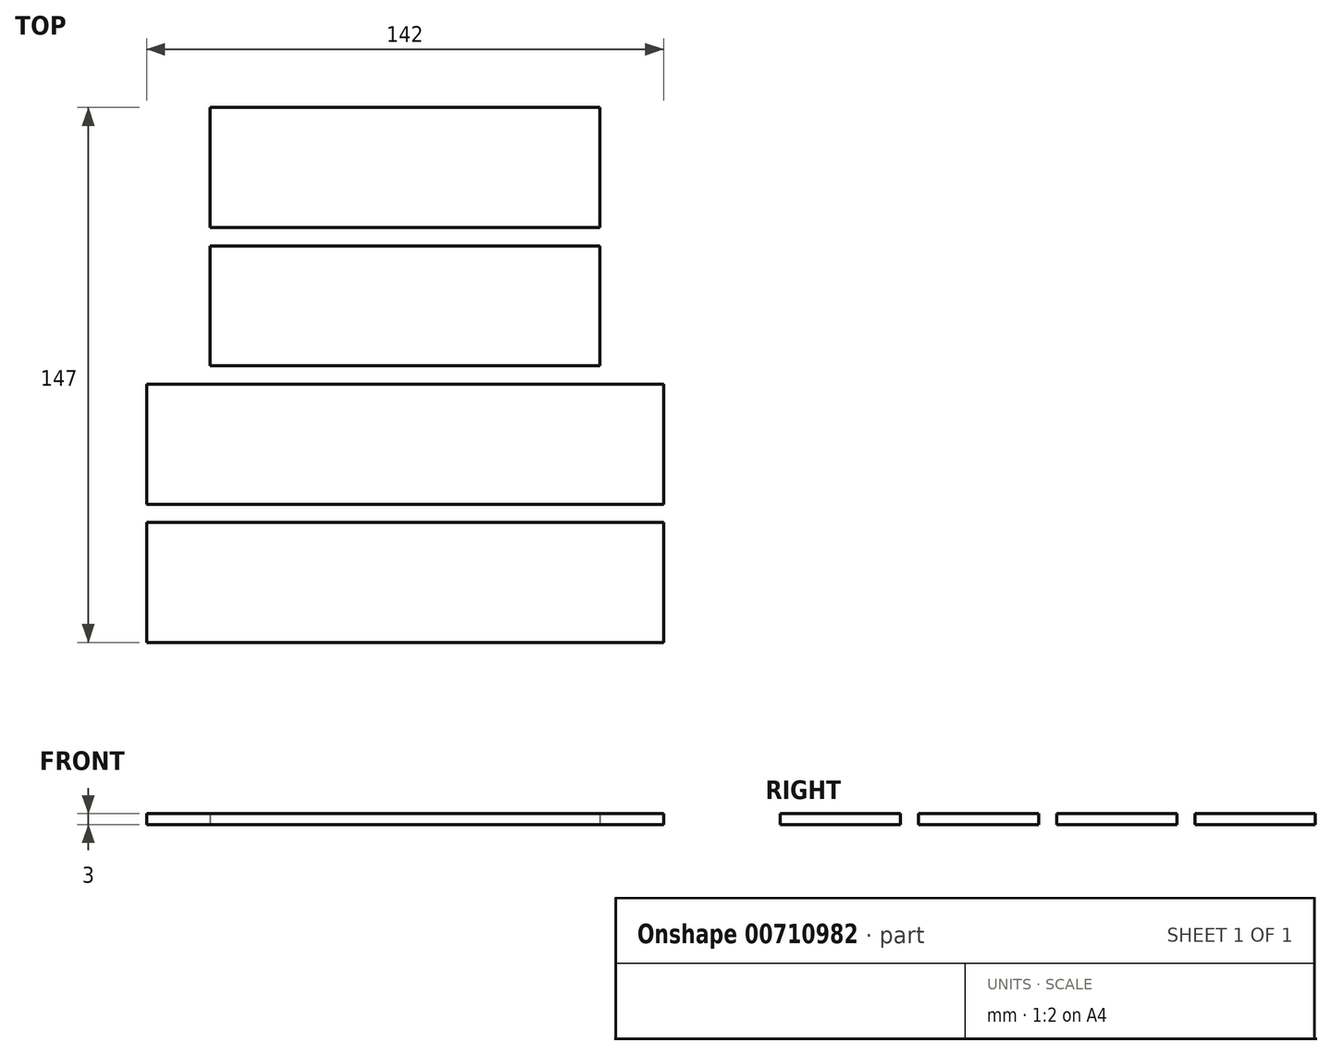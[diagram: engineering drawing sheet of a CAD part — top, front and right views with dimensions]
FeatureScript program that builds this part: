
annotation { "Feature Type Name" : "Feature", "Feature Type Description" : "" }
export const myFeature = defineFeature(function(context is Context, id is Id, definition is map)
    precondition{}
    {
        {
            var Q0;
            Q0=qCreatedBy(makeId("Top.planeOp"),FACE);
            var sketch = newSketch(context, id + "F0", { "sketchPlane" : qUnion([Q0])});
            skLineSegment(sketch, "E0.bottom", {"start": v(-53.5, 51.54) * mm, "end": v(53.5, 51.54) * mm});
            skLineSegment(sketch, "E0.top", {"start": v(-53.5, 84.54) * mm, "end": v(53.5, 84.54) * mm});
            skLineSegment(sketch, "E0.left", {"start": v(-53.5, 51.54) * mm, "end": v(-53.5, 84.54) * mm});
            skLineSegment(sketch, "E0.right", {"start": v(53.5, 51.54) * mm, "end": v(53.5, 84.54) * mm});
            skPoint(sketch, "E0.middle", {"position": v(0, 68.04) * mm});
            skLineSegment(sketch, "E1.bottom", {"start": v(-53.5, 46.54) * mm, "end": v(53.5, 46.54) * mm});
            skLineSegment(sketch, "E1.top", {"start": v(-53.5, 13.54) * mm, "end": v(53.5, 13.54) * mm});
            skLineSegment(sketch, "E1.left", {"start": v(-53.5, 46.54) * mm, "end": v(-53.5, 13.54) * mm});
            skLineSegment(sketch, "E1.right", {"start": v(53.5, 46.54) * mm, "end": v(53.5, 13.54) * mm});
            skPoint(sketch, "E1.middle", {"position": v(0, 30.04) * mm});
            skLineSegment(sketch, "E2.bottom", {"start": v(-71, 8.54) * mm, "end": v(71, 8.54) * mm});
            skLineSegment(sketch, "E2.top", {"start": v(-71, -24.46) * mm, "end": v(71, -24.46) * mm});
            skLineSegment(sketch, "E2.left", {"start": v(-71, 8.54) * mm, "end": v(-71, -24.46) * mm});
            skLineSegment(sketch, "E2.right", {"start": v(71, 8.54) * mm, "end": v(71, -24.46) * mm});
            skPoint(sketch, "E2.middle", {"position": v(0, -7.96) * mm});
            skLineSegment(sketch, "E3.bottom", {"start": v(-71, -29.46) * mm, "end": v(71, -29.46) * mm});
            skLineSegment(sketch, "E3.top", {"start": v(-71, -62.46) * mm, "end": v(71, -62.46) * mm});
            skLineSegment(sketch, "E3.left", {"start": v(-71, -29.46) * mm, "end": v(-71, -62.46) * mm});
            skLineSegment(sketch, "E3.right", {"start": v(71, -29.46) * mm, "end": v(71, -62.46) * mm});
            skPoint(sketch, "E3.middle", {"position": v(0, -45.96) * mm});
            skSolve(sketch);
        }
        {
            var Q0;
            Q0 = qSketchRegion(id + "F0", true);
            extrude(context, id + "F1", {"entities" : qUnion([Q0]), "depth" : 3 * mm, "offsetDistance" : 25 * mm});
        }
    });
